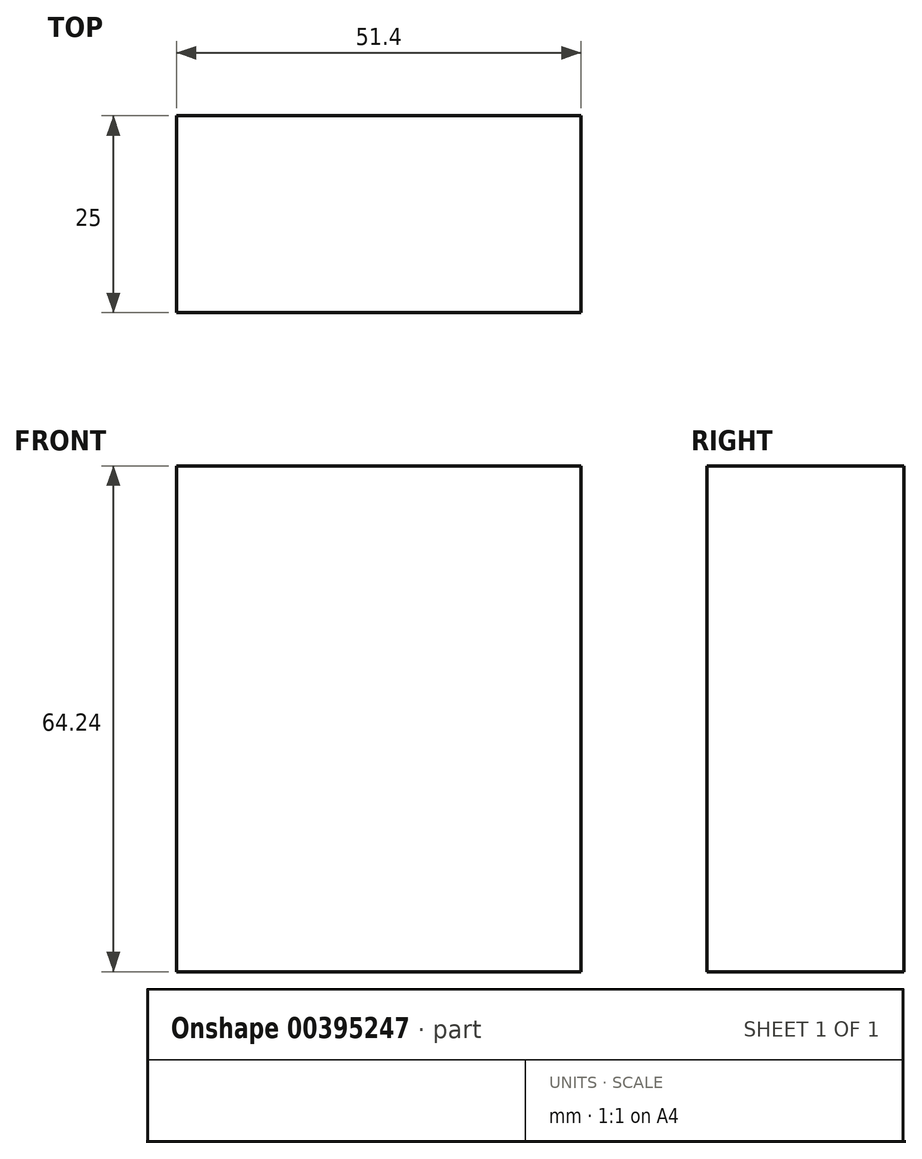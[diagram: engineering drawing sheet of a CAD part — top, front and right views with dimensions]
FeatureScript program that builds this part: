
annotation { "Feature Type Name" : "Feature", "Feature Type Description" : "" }
export const myFeature = defineFeature(function(context is Context, id is Id, definition is map)
    precondition{}
    {
        {
            var Q0;
            Q0=qCreatedBy(makeId("Front.planeOp"),FACE);
            var sketch = newSketch(context, id + "F0", { "sketchPlane" : qUnion([Q0])});
            skLineSegment(sketch, "E0.bottom", {"start": v(-94.46, -19.26) * mm, "end": v(-43.06, -19.26) * mm});
            skLineSegment(sketch, "E0.top", {"start": v(-94.46, 44.98) * mm, "end": v(-43.06, 44.98) * mm});
            skLineSegment(sketch, "E0.left", {"start": v(-94.46, -19.26) * mm, "end": v(-94.46, 44.98) * mm});
            skLineSegment(sketch, "E0.right", {"start": v(-43.06, -19.26) * mm, "end": v(-43.06, 44.98) * mm});
            skPoint(sketch, "E0.middle", {"position": v(-68.76, 12.86) * mm});
            skSolve(sketch);
        }
        {
            var Q0;
            Q0=makeQuery(id+"F0.imprint","IMPRINT",FACE,{"disambiguationData":[TD([[makeQuery(id+"F0.imprint","IMPRINT",EDGE,{"derivedFrom":sQuery(id+"F0.wireOp",EDGE,"E0.bottom")}),1.0]])]});
            extrude(context, id + "F1", {"entities" : qUnion([Q0]), "depth" : 25 * mm});
        }
    });
